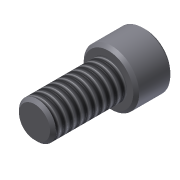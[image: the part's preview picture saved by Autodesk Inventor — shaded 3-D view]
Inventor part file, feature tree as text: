
AUTODESK INVENTOR PART (.ipt)
format: ipt  version: 2013 (Build 170138000, 138)  size: 114,176 bytes
history: native  units: in
note: dims shown in document units (in); Inventor stores cm internally (conversion verified against a paired STEP export)
features: extrude x3, sketch x3, other x1, chamfer x1, thread x1
ambient origin geometry x8: Origin, YZ Plane, XZ Plane, XY Plane, X Axis, Y Axis, Z Axis, Center Point
bodies: Solid1 (feature_tree)
feature tree (9):
  other  "14-20 SHCS x500"
  extrude  "Extrusion1"  Depth=0.5in TaperAngle=0.0deg
  extrude  "Extrusion2"  Depth=0.25in TaperAngle=0.0deg
  extrude  "Extrusion3"  Depth=0.125in TaperAngle=0.0deg
  chamfer  "Chamfer1"  Distance=0.02in Angle=45.0deg
  thread  "Thread1"  [1 undecoded]
  sketch  "Sketch1"  dims[d0=0.25in d1=0.5in d2=0.0in]
  sketch  "Sketch2"  dims[d3=0.375in d4=0.25in d5=0.0in]
  sketch  "Sketch3"  dims[d6=0.1875in d7=0.125in d8=0.0in d9=0.02in d10=0.125in d11=45.0deg d12=1.0in d13=0.0in]
note: 1 required parameter value undecoded (feature->parameter linkage not recoverable at this tier; creation-order binding heuristic only, values carry confidence <= 0.55)
